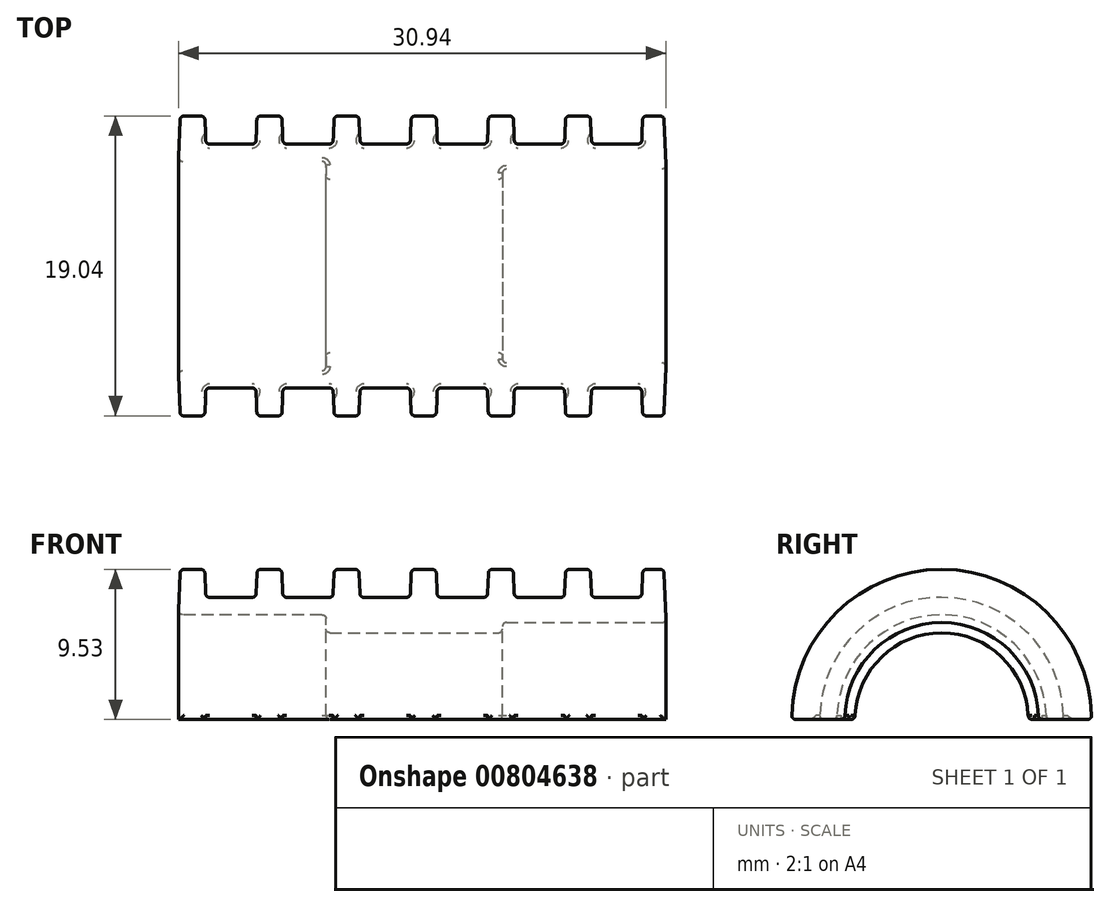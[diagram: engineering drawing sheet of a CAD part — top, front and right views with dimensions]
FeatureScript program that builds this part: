
annotation { "Feature Type Name" : "Feature", "Feature Type Description" : "" }
export const myFeature = defineFeature(function(context is Context, id is Id, definition is map)
    precondition{}
    {
        {
            var Q0;
            Q0=qCreatedBy(makeId("Right.planeOp"),FACE);
            var sketch = newSketch(context, id + "F0", { "sketchPlane" : qUnion([Q0])});
            skCircle(sketch, "E0", {"center": v(0, 0) * mm, "radius": 9.53 * mm});
            skCircle(sketch, "E1", {"center": v(0, 0) * mm, "radius": 5.5 * mm});
            skSolve(sketch);
        }
        {
            var Q0;
            Q0 = qSketchRegion(id + "F0", true);
            extrude(context, id + "F1", {"entities" : qUnion([Q0]), "oppositeDirection" : true, "depth" : 31 * mm, "offsetDistance" : 25 * mm});
        }
        {
            var Q0;
            Q0=makeQuery(id+"F1.opExtrude","CAP_FACE",FACE,{"disambiguationData":[OSD([sQuery(id+"F0.wireOp",EDGE,"E0"),sQuery(id+"F0.wireOp",EDGE,"E1")])],"isStart":true});
            var sketch = newSketch(context, id + "F2", { "sketchPlane" : qUnion([Q0])});
            skCircle(sketch, "E2", {"center": v(0, 0) * mm, "radius": 6.15 * mm});
            skSolve(sketch);
        }
        {
            var Q0;
            Q0 = qSketchRegion(id + "F2", true);
            extrude(context, id + "F3", {"entities" : qUnion([Q0]), "operationType" : NewBodyOperationType.REMOVE, "oppositeDirection" : true, "depth" : 10.4 * mm, "offsetDistance" : 25 * mm});
        }
        {
            var Q0;
            Q0=makeQuery(id+"F1.opExtrude","CAP_FACE",FACE,{"disambiguationData":[OSD([sQuery(id+"F0.wireOp",EDGE,"E0"),sQuery(id+"F0.wireOp",EDGE,"E1")])],"isStart":false});
            var sketch = newSketch(context, id + "F4", { "sketchPlane" : qUnion([Q0])});
            skCircle(sketch, "E3", {"center": v(0, 0) * mm, "radius": 6.65 * mm});
            skSolve(sketch);
        }
        {
            var Q0;
            Q0 = qSketchRegion(id + "F4", true);
            extrude(context, id + "F5", {"entities" : qUnion([Q0]), "operationType" : NewBodyOperationType.REMOVE, "oppositeDirection" : true, "depth" : 9.4 * mm, "offsetDistance" : 25 * mm});
        }
        {
            var Q0;
            Q0=qCreatedBy(makeId("Front.planeOp"),FACE);
            var sketch = newSketch(context, id + "F6", { "sketchPlane" : qUnion([Q0])});
            skLineSegment(sketch, "E4.bottom", {"start": v(-1.45, 10.75) * mm, "end": v(-4.85, 10.75) * mm});
            skLineSegment(sketch, "E4.top", {"start": v(-1.55, 7.75) * mm, "end": v(-4.74, 7.75) * mm});
            skLineSegment(sketch, "E4.left", {"start": v(-1.45, 10.75) * mm, "end": v(-1.55, 7.75) * mm});
            skLineSegment(sketch, "E5", {"start": v(0, 0) * mm, "end": v(-32.08, 0) * mm, "construction": true});
            skLineSegment(sketch, "E6", {"start": v(-4.85, 10.75) * mm, "end": v(-4.74, 7.75) * mm});
            skLineSegment(sketch, "E7.1.0.0", {"start": v(-6.45, 7.75) * mm, "end": v(-9.64, 7.75) * mm});
            skLineSegment(sketch, "E7.1.0.1", {"start": v(-9.75, 10.75) * mm, "end": v(-9.64, 7.75) * mm});
            skLineSegment(sketch, "E7.1.0.2", {"start": v(-6.35, 10.75) * mm, "end": v(-9.75, 10.75) * mm});
            skLineSegment(sketch, "E7.1.0.3", {"start": v(-6.35, 10.75) * mm, "end": v(-6.45, 7.75) * mm});
            skLineSegment(sketch, "E7.2.0.0", {"start": v(-11.35, 7.75) * mm, "end": v(-14.54, 7.75) * mm});
            skLineSegment(sketch, "E7.2.0.1", {"start": v(-14.65, 10.75) * mm, "end": v(-14.54, 7.75) * mm});
            skLineSegment(sketch, "E7.2.0.2", {"start": v(-11.25, 10.75) * mm, "end": v(-14.65, 10.75) * mm});
            skLineSegment(sketch, "E7.2.0.3", {"start": v(-11.25, 10.75) * mm, "end": v(-11.35, 7.75) * mm});
            skLineSegment(sketch, "E7.3.0.0", {"start": v(-16.25, 7.75) * mm, "end": v(-19.44, 7.75) * mm});
            skLineSegment(sketch, "E7.3.0.1", {"start": v(-19.55, 10.75) * mm, "end": v(-19.44, 7.75) * mm});
            skLineSegment(sketch, "E7.3.0.2", {"start": v(-16.15, 10.75) * mm, "end": v(-19.55, 10.75) * mm});
            skLineSegment(sketch, "E7.3.0.3", {"start": v(-16.15, 10.75) * mm, "end": v(-16.25, 7.75) * mm});
            skLineSegment(sketch, "E7.4.0.0", {"start": v(-21.15, 7.75) * mm, "end": v(-24.34, 7.75) * mm});
            skLineSegment(sketch, "E7.4.0.1", {"start": v(-24.45, 10.75) * mm, "end": v(-24.34, 7.75) * mm});
            skLineSegment(sketch, "E7.4.0.2", {"start": v(-21.05, 10.75) * mm, "end": v(-24.45, 10.75) * mm});
            skLineSegment(sketch, "E7.4.0.3", {"start": v(-21.05, 10.75) * mm, "end": v(-21.15, 7.75) * mm});
            skLineSegment(sketch, "E7.5.0.0", {"start": v(-26.05, 7.75) * mm, "end": v(-29.24, 7.75) * mm});
            skLineSegment(sketch, "E7.5.0.1", {"start": v(-29.35, 10.75) * mm, "end": v(-29.24, 7.75) * mm});
            skLineSegment(sketch, "E7.5.0.2", {"start": v(-25.95, 10.75) * mm, "end": v(-29.35, 10.75) * mm});
            skLineSegment(sketch, "E7.5.0.3", {"start": v(-25.95, 10.75) * mm, "end": v(-26.05, 7.75) * mm});
            skLineSegment(sketch, "E7.direction1", {"start": v(-4.74, 7.75) * mm, "end": v(-9.64, 7.75) * mm, "construction": true});
            skLineSegment(sketch, "E8", {"start": v(-0.17, 10.75) * mm, "end": v(0, 5.75) * mm});
            skLineSegment(sketch, "E9", {"start": v(0, 5.75) * mm, "end": v(4.83, 5.75) * mm});
            skLineSegment(sketch, "E10", {"start": v(4.83, 5.75) * mm, "end": v(4.83, 10.75) * mm});
            skLineSegment(sketch, "E11", {"start": v(4.83, 10.75) * mm, "end": v(-0.17, 10.75) * mm});
            skLineSegment(sketch, "E12", {"start": v(-15.5, 16.54) * mm, "end": v(-15.5, -14.8) * mm, "construction": true});
            skLineSegment(sketch, "E13.MirrorCS", {"start": v(-35.83, 10.75) * mm, "end": v(-30.83, 10.75) * mm});
            skLineSegment(sketch, "E14.MirrorCS", {"start": v(-31, 5.75) * mm, "end": v(-35.83, 5.75) * mm});
            skLineSegment(sketch, "E15.MirrorCS", {"start": v(-30.83, 10.75) * mm, "end": v(-31, 5.75) * mm});
            skLineSegment(sketch, "E16.MirrorCS", {"start": v(-35.83, 5.75) * mm, "end": v(-35.83, 10.75) * mm});
            skSolve(sketch);
        }
        {
            var Q0;
            Q0 = qSketchRegion(id + "F6", true);
            var Q1;
            Q1=sQuery(id+"F6.wireOp",EDGE,"E5");
            revolve(context, id + "F7", {"operationType" : NewBodyOperationType.REMOVE, "surfaceOperationType" : NewSurfaceOperationType.NEW, "entities" : qUnion([Q0]), "axis" : qUnion([Q1]), "revolveType" : RevolveType.FULL, "oppositeDirection" : true});
        }
        {
            var Q0;
            Q0=qCreatedBy(makeId("Right.planeOp"),FACE);
            var sketch = newSketch(context, id + "F8", { "sketchPlane" : qUnion([Q0])});
            skLineSegment(sketch, "E17.bottom", {"start": v(-12.83, 0) * mm, "end": v(15.16, 0) * mm});
            skLineSegment(sketch, "E17.top", {"start": v(-12.83, -13.34) * mm, "end": v(15.16, -13.34) * mm});
            skLineSegment(sketch, "E17.left", {"start": v(-12.83, 0) * mm, "end": v(-12.83, -13.34) * mm});
            skLineSegment(sketch, "E17.right", {"start": v(15.16, 0) * mm, "end": v(15.16, -13.34) * mm});
            skSolve(sketch);
        }
        {
            var Q0;
            Q0=makeQuery(id+"F8.imprint","IMPRINT",FACE,{"disambiguationData":[TD([[makeQuery(id+"F8.imprint","IMPRINT",EDGE,{"derivedFrom":sQuery(id+"F8.wireOp",EDGE,"E17.bottom")}),-1.0]])]});
            extrude(context, id + "F9", {"entities" : qUnion([Q0]), "operationType" : NewBodyOperationType.REMOVE, "endBound" : BoundingType.THROUGH_ALL, "oppositeDirection" : true, "depth" : 25 * mm, "offsetDistance" : 25 * mm});
        }
        {
            var Q0;
            Q0=makeQuery(id+"F7.boolean.opBoolean","SPLIT",FACE,{"disambiguationData":[TD([makeQuery(id+"F7.opRevolve","SWEPT_FACE",FACE,{"disambiguationData":[OSD([sQuery(id+"F6.wireOp",EDGE,"E7.5.0.1")])]})])],"derivedFrom":makeQuery(id+"F1.opExtrude","SWEPT_FACE",FACE,{"disambiguationData":[OSD([sQuery(id+"F0.wireOp",EDGE,"E0")])]})});
            var Q1;
            Q1=makeQuery(id+"F7.boolean.opBoolean","COPY",FACE,{"derivedFrom":makeQuery(id+"F7.opRevolve","SWEPT_FACE",FACE,{"disambiguationData":[OSD([sQuery(id+"F6.wireOp",EDGE,"E7.5.0.0")])]})});
            var Q2;
            Q2=makeQuery(id+"F7.boolean.opBoolean","SPLIT",FACE,{"disambiguationData":[TD([makeQuery(id+"F7.opRevolve","SWEPT_FACE",FACE,{"disambiguationData":[OSD([sQuery(id+"F6.wireOp",EDGE,"E7.4.0.1")])]})])],"derivedFrom":makeQuery(id+"F1.opExtrude","SWEPT_FACE",FACE,{"disambiguationData":[OSD([sQuery(id+"F0.wireOp",EDGE,"E0")])]})});
            var Q3;
            Q3=makeQuery(id+"F7.boolean.opBoolean","COPY",FACE,{"derivedFrom":makeQuery(id+"F7.opRevolve","SWEPT_FACE",FACE,{"disambiguationData":[OSD([sQuery(id+"F6.wireOp",EDGE,"E7.4.0.0")])]})});
            var Q4;
            Q4=makeQuery(id+"F7.boolean.opBoolean","SPLIT",FACE,{"disambiguationData":[TD([makeQuery(id+"F7.opRevolve","SWEPT_FACE",FACE,{"disambiguationData":[OSD([sQuery(id+"F6.wireOp",EDGE,"E7.3.0.1")])]})])],"derivedFrom":makeQuery(id+"F1.opExtrude","SWEPT_FACE",FACE,{"disambiguationData":[OSD([sQuery(id+"F0.wireOp",EDGE,"E0")])]})});
            var Q5;
            Q5=makeQuery(id+"F7.boolean.opBoolean","COPY",FACE,{"derivedFrom":makeQuery(id+"F7.opRevolve","SWEPT_FACE",FACE,{"disambiguationData":[OSD([sQuery(id+"F6.wireOp",EDGE,"E7.3.0.0")])]})});
            var Q6;
            Q6=makeQuery(id+"F7.boolean.opBoolean","SPLIT",FACE,{"disambiguationData":[TD([makeQuery(id+"F7.opRevolve","SWEPT_FACE",FACE,{"disambiguationData":[OSD([sQuery(id+"F6.wireOp",EDGE,"E7.2.0.1")])]})])],"derivedFrom":makeQuery(id+"F1.opExtrude","SWEPT_FACE",FACE,{"disambiguationData":[OSD([sQuery(id+"F0.wireOp",EDGE,"E0")])]})});
            var Q7;
            Q7=makeQuery(id+"F7.boolean.opBoolean","COPY",FACE,{"derivedFrom":makeQuery(id+"F7.opRevolve","SWEPT_FACE",FACE,{"disambiguationData":[OSD([sQuery(id+"F6.wireOp",EDGE,"E7.2.0.0")])]})});
            var Q8;
            Q8=makeQuery(id+"F7.boolean.opBoolean","SPLIT",FACE,{"disambiguationData":[TD([makeQuery(id+"F7.opRevolve","SWEPT_FACE",FACE,{"disambiguationData":[OSD([sQuery(id+"F6.wireOp",EDGE,"E7.1.0.1")])]})])],"derivedFrom":makeQuery(id+"F1.opExtrude","SWEPT_FACE",FACE,{"disambiguationData":[OSD([sQuery(id+"F0.wireOp",EDGE,"E0")])]})});
            var Q9;
            Q9=makeQuery(id+"F7.boolean.opBoolean","COPY",FACE,{"derivedFrom":makeQuery(id+"F7.opRevolve","SWEPT_FACE",FACE,{"disambiguationData":[OSD([sQuery(id+"F6.wireOp",EDGE,"E7.1.0.0")])]})});
            var Q10;
            Q10=makeQuery(id+"F7.boolean.opBoolean","SPLIT",FACE,{"disambiguationData":[TD([makeQuery(id+"F7.opRevolve","SWEPT_FACE",FACE,{"disambiguationData":[OSD([sQuery(id+"F6.wireOp",EDGE,"E6")])]})])],"derivedFrom":makeQuery(id+"F1.opExtrude","SWEPT_FACE",FACE,{"disambiguationData":[OSD([sQuery(id+"F0.wireOp",EDGE,"E0")])]})});
            var Q11;
            Q11=makeQuery(id+"F7.boolean.opBoolean","COPY",FACE,{"derivedFrom":makeQuery(id+"F7.opRevolve","SWEPT_FACE",FACE,{"disambiguationData":[OSD([sQuery(id+"F6.wireOp",EDGE,"E4.top")])]})});
            var Q12;
            Q12=makeQuery(id+"F7.boolean.opBoolean","SPLIT",FACE,{"disambiguationData":[TD([makeQuery(id+"F7.opRevolve","SWEPT_FACE",FACE,{"disambiguationData":[OSD([sQuery(id+"F6.wireOp",EDGE,"E4.left")])]})])],"derivedFrom":makeQuery(id+"F1.opExtrude","SWEPT_FACE",FACE,{"disambiguationData":[OSD([sQuery(id+"F0.wireOp",EDGE,"E0")])]})});
            var Q13;
            Q13=makeQuery(id+"F1.opExtrude","SWEPT_FACE",FACE,{"disambiguationData":[OSD([sQuery(id+"F0.wireOp",EDGE,"E1")])]});
            var Q14;
            Q14=makeQuery(id+"F5.boolean.opBoolean","COPY",FACE,{"derivedFrom":makeQuery(id+"F5.opExtrude","SWEPT_FACE",FACE,{"disambiguationData":[OSD([sQuery(id+"F4.wireOp",EDGE,"E3")])]})});
            var Q15;
            Q15=makeQuery(id+"F5.boolean.opBoolean","COPY",FACE,{"derivedFrom":makeQuery(id+"F5.opExtrude","CAP_FACE",FACE,{"disambiguationData":[OSD([sQuery(id+"F4.wireOp",EDGE,"E3")])],"isStart":false})});
            var Q16;
            Q16=makeQuery(id+"F3.boolean.opBoolean","COPY",FACE,{"derivedFrom":makeQuery(id+"F3.opExtrude","SWEPT_FACE",FACE,{"disambiguationData":[OSD([sQuery(id+"F2.wireOp",EDGE,"E2")])]})});
            var Q17;
            Q17=makeQuery(id+"F3.boolean.opBoolean","COPY",FACE,{"derivedFrom":makeQuery(id+"F3.opExtrude","CAP_FACE",FACE,{"disambiguationData":[OSD([sQuery(id+"F2.wireOp",EDGE,"E2")])],"isStart":false})});
            fillet(context, id + "F10", {"entities" : qUnion([Q0, Q1, Q2, Q3, Q4, Q5, Q6, Q7, Q8, Q9, Q10, Q11, Q12, Q13, Q14, Q15, Q16, Q17]), "radius" : .25 * mm, "tangentPropagation" : true, "allowEdgeOverflow" : false});
        }
    });
